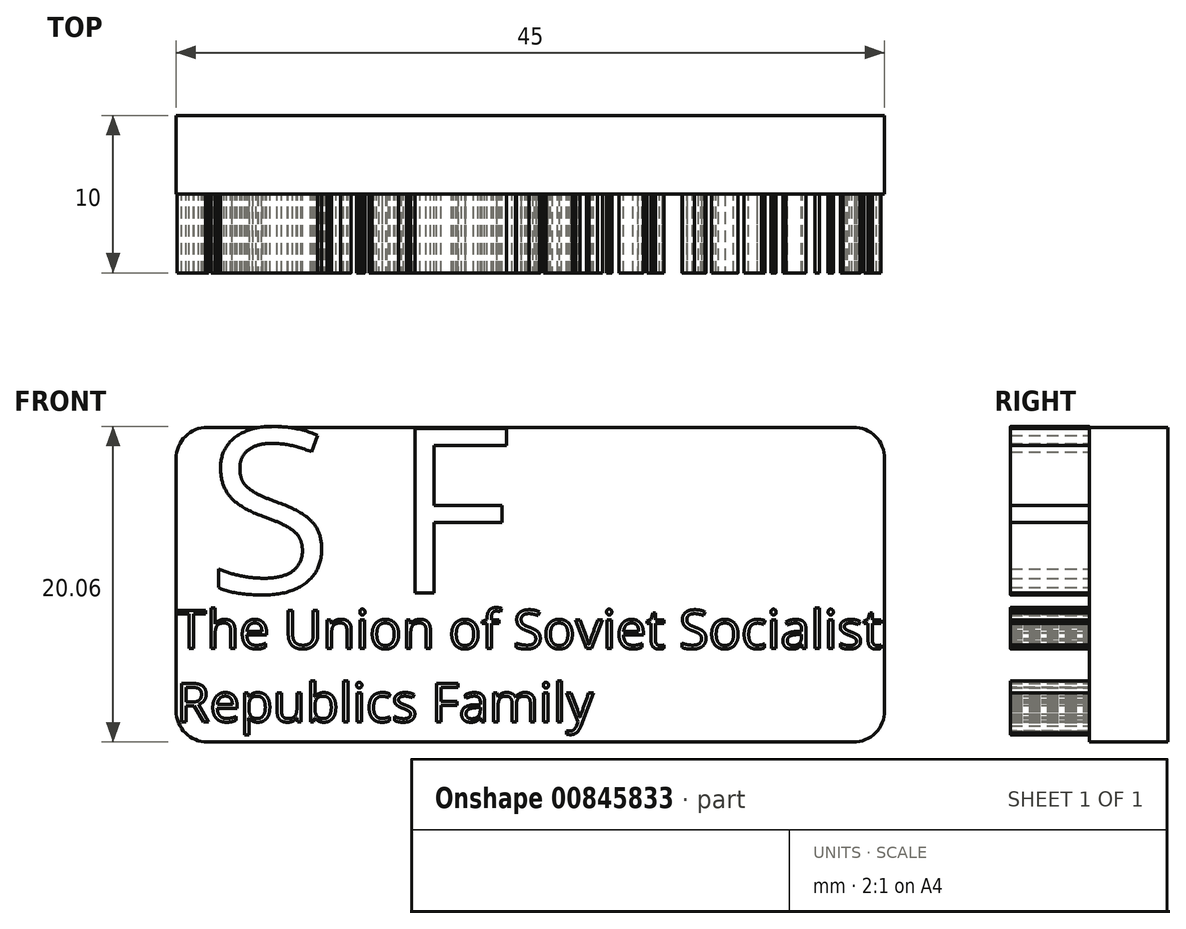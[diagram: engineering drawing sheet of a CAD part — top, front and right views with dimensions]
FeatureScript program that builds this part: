
annotation { "Feature Type Name" : "Feature", "Feature Type Description" : "" }
export const myFeature = defineFeature(function(context is Context, id is Id, definition is map)
    precondition{}
    {
        {
            var Q0;
            Q0=qCreatedBy(makeId("Front.planeOp"),FACE);
            var sketch = newSketch(context, id + "F0", { "sketchPlane" : qUnion([Q0])});
            skLineSegment(sketch, "E0.bottom", {"start": v(0, 0) * mm, "end": v(45, 0) * mm});
            skLineSegment(sketch, "E0.top", {"start": v(0, 20) * mm, "end": v(45, 20) * mm});
            skLineSegment(sketch, "E0.left", {"start": v(0, 0) * mm, "end": v(0, 20) * mm});
            skLineSegment(sketch, "E0.right", {"start": v(45, 0) * mm, "end": v(45, 20) * mm});
            skSolve(sketch);
        }
        {
            var Q0;
            Q0 = qSketchRegion(id + "F0", true);
            extrude(context, id + "F1", {"entities" : qUnion([Q0]), "depth" : 5 * mm, "offsetDistance" : 25 * mm});
        }
        {
            var Q0;
            Q0=makeQuery(id+"F1.opExtrude","CAP_FACE",FACE,{"disambiguationData":[OSD([sQuery(id+"F0.wireOp",EDGE,"E0.bottom"),sQuery(id+"F0.wireOp",EDGE,"E0.top"),sQuery(id+"F0.wireOp",EDGE,"E0.left"),sQuery(id+"F0.wireOp",EDGE,"E0.right")])],"isStart":false});
            var sketch = newSketch(context, id + "F2", { "sketchPlane" : qUnion([Q0])});
            skText(sketch, "E1", { "text": "S F", "fontName": "OpenSans-Regular.ttf"});
            const initialGuessF2  = {"E1": [0.00193, 0.00949, 1, 0, 0.01051]};
            skSetInitialGuess(sketch, initialGuessF2);
            skSolve(sketch);
        }
        {
            var Q0;
            Q0 = qSketchRegion(id + "F2", true);
            extrude(context, id + "F3", {"entities" : qUnion([Q0]), "operationType" : NewBodyOperationType.ADD, "depth" : 5 * mm, "offsetDistance" : 25 * mm});
        }
        {
            var Q0;
            Q0=makeQuery(id+"F1.opExtrude","CAP_FACE",FACE,{"disambiguationData":[OSD([sQuery(id+"F0.wireOp",EDGE,"E0.bottom"),sQuery(id+"F0.wireOp",EDGE,"E0.top"),sQuery(id+"F0.wireOp",EDGE,"E0.left"),sQuery(id+"F0.wireOp",EDGE,"E0.right")])],"isStart":false});
            var sketch = newSketch(context, id + "F4", { "sketchPlane" : qUnion([Q0])});
            skText(sketch, "E2", { "text": "The Union of Soviet Socialist\nRepublics Family", "fontName": "OpenSans-Regular.ttf"});
            const initialGuessF4  = {"E2": [2e-05, 0.00594, 1, 0, 0.00246]};
            skSetInitialGuess(sketch, initialGuessF4);
            skSolve(sketch);
        }
        {
            var Q0;
            Q0 = qSketchRegion(id + "F4", true);
            extrude(context, id + "F5", {"entities" : qUnion([Q0]), "operationType" : NewBodyOperationType.ADD, "depth" : 5 * mm, "offsetDistance" : 25 * mm});
        }
        {
            var Q0;
            Q0=makeQuery(id+"F1.opExtrude","SWEPT_EDGE",EDGE,{"disambiguationData":[OSD([sQuery(id+"F0.wireOp",EDGE,"E0.top"),sQuery(id+"F0.wireOp",EDGE,"E0.left")])]});
            var Q1;
            Q1=makeQuery(id+"F1.opExtrude","SWEPT_EDGE",EDGE,{"disambiguationData":[OSD([sQuery(id+"F0.wireOp",EDGE,"E0.top"),sQuery(id+"F0.wireOp",EDGE,"E0.right")])]});
            var Q2;
            Q2=makeQuery(id+"F1.opExtrude","SWEPT_EDGE",EDGE,{"disambiguationData":[OSD([sQuery(id+"F0.wireOp",EDGE,"E0.bottom"),sQuery(id+"F0.wireOp",EDGE,"E0.right")])]});
            var Q3;
            Q3=makeQuery(id+"F1.opExtrude","SWEPT_EDGE",EDGE,{"disambiguationData":[OSD([sQuery(id+"F0.wireOp",EDGE,"E0.bottom"),sQuery(id+"F0.wireOp",EDGE,"E0.left")])]});
            fillet(context, id + "F6", {"entities" : qUnion([Q0, Q1, Q2, Q3]), "radius" : 2 * mm, "tangentPropagation" : true, "allowEdgeOverflow" : false});
        }
    });
